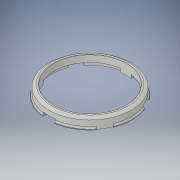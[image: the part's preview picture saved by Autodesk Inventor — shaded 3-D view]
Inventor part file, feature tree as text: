
AUTODESK INVENTOR PART (.ipt)
format: ipt  version: 2018 (Build 220112000, 112)  size: 474,112 bytes
history: native  units: mm
features: reference x28, sketch x15, projected_geometry x12, extrude x7, other x7, sweep x5, fillet x5, chamfer x3, pattern_circular x2
ambient origin geometry x8: Origin, YZ Plane, XZ Plane, XY Plane, X Axis, Y Axis, Z Axis, Center Point
bodies: Volumenkörper1 (feature_tree)
feature tree (84):
  extrude  "Extrusion1"  Depth=2.0mm TaperAngle=45.0deg
  chamfer  "Fase1"  Distance=2.0mm
  extrude  "Extrusion4"  TaperAngle=0.0deg  [1 undecoded]
  sweep  "Sweeping4"
  sketch  "Skizze16"  dims[d29=23.0mm]
  sketch  "Skizze17"  dims[d30=2.0mm d31=0.0mm]
  sweep  "Sweeping5"
  fillet  "Rundung4"  Radius=0.5mm
  fillet  "Rundung5"  Radius=0.1mm
  extrude  "Extrusion6"  Depth=2.0mm TaperAngle=45.0deg
  pattern_circular  "Runde Anordnung1"  [2 undecoded]
  extrude  "Extrusion7"  Depth=2.0mm
  chamfer  "Fase3"  Distance=62.65732mm
  extrude  "Extrusion8"  Depth=2.0mm
  pattern_circular  "Runde Anordnung2"  [2 undecoded]
  extrude  "Extrusion2"  Depth=2.0mm TaperAngle=0.0deg
  sketch  "Skizze3"  dims[d5=0.2mm]
  sketch  "Skizze4"  dims[d6=0.2mm]
  sketch  "Skizze6"  dims[d7=0.2mm d8=2.0mm d9=0.0mm]
  sweep  "Sweeping1"
  sweep  "Sweeping2"
  sweep  "Sweeping3"
  chamfer  "Fase2"  Distance=0.5mm
  fillet  "Rundung1"  Radius=0.5mm
  fillet  "Rundung2"  Radius=60.0mm
  extrude  "Extrusion3"  Depth=2.0mm
  fillet  "Rundung3"  Radius=0.5mm
  sketch  "Skizze10"  dims[d20=0.0mm d21=0.0mm d22=0.25mm d23=2.0mm d24=45.0deg]
  sketch  "Skizze1"  dims[d0=4.0mm d1=0.0mm d2=0.2mm d3=2.0mm d4=45.0deg]
  reference  "Referenz1"
  reference  "Referenz2"
  reference  "Referenz3"
  reference  "Referenz4"
  reference  "Referenz5"
  reference  "Referenz6"
  reference  "Referenz7"
  reference  "Referenz8"
  reference  "Referenz9"
  reference  "Referenz10"
  reference  "Referenz11"
  reference  "Referenz12"
  reference  "Referenz13"
  reference  "Referenz14"
  reference  "Referenz15"
  reference  "Referenz16"
  reference  "Referenz17"
  reference  "Referenz18"
  reference  "Referenz19"
  reference  "Referenz20"
  reference  "Referenz21"
  reference  "Referenz22"
  reference  "Referenz23"
  reference  "Referenz24"
  reference  "Referenz25"
  other  "3D-Skizze1"
  sketch  "Skizze7"  dims[d10=0.1mm d11=0.0mm d12=0.0mm]
  projected_geometry  "Projizierte Kontur1"
  reference  "Referenz26"
  other  "3D-Skizze2"
  sketch  "Skizze8"  dims[d13=0.1mm d14=0.5mm]
  projected_geometry  "Projizierte Kontur2"
  reference  "Referenz27"
  other  "3D-Skizze3"
  sketch  "Skizze9"  dims[d15=0.5mm d16=0.0mm d17=0.0mm d18=0.5mm d19=0.1mm]
  projected_geometry  "Projizierte Kontur3"
  projected_geometry  "Projizierte Kontur4"
  projected_geometry  "Projizierte Kontur5"
  projected_geometry  "Projizierte Kontur6"
  sketch  "Skizze12"  dims[d25=0.25mm]
  projected_geometry  "Projizierte Kontur7"
  sketch  "Skizze13"  dims[d26=0.25mm]
  reference  "Referenz29"
  sketch  "Skizze14"  dims[d27=23.0mm]
  sketch  "Skizze15"  dims[d28=23.0mm]
  projected_geometry  "Projizierte Kontur8"
  projected_geometry  "Projizierte Kontur9"
  projected_geometry  "Projizierte Kontur10"
  projected_geometry  "Projizierte Kontur11"
  other  "3D-Skizze4"
  sketch  "Skizze18"  dims[d32=1.25mm d33=0.174533mm d34=0.174533mm d36=62.65732mm d37=0.174533mm d38=0.174533mm d39=2.0mm d40=0.0mm d43=2.0mm d44=0.0mm d45=0.5mm d46=0.4mm d47=0.5mm d48=0.5mm d49=60.0mm d50=360.0deg d52=0.5mm d53=0.5mm d54=0.0mm d55=0.0mm d56=0.2mm d57=0.0mm d58=0.0mm d59=1.0mm d60=0.25mm d61=2.0mm d62=0.0mm d63=1.25mm d64=1.75mm d65=45.0deg d66=1.0mm d67=2.0mm d68=0.0mm d69=30.0mm d70=360.0deg]
  projected_geometry  "Projizierte Kontur12"
  parser-record x1  (decoder bookkeeping rows leaked as tree rows — omitted from the tree; the rows remain in map.json)
  other  "VolumeKnob.iam"
  other  "Oberbau:1"
note: 5 required parameter values undecoded (feature->parameter linkage not recoverable at this tier; creation-order binding heuristic only, values carry confidence <= 0.55)
note: 1 file-system path scrubbed to <path> (originals preserved in map.json)
